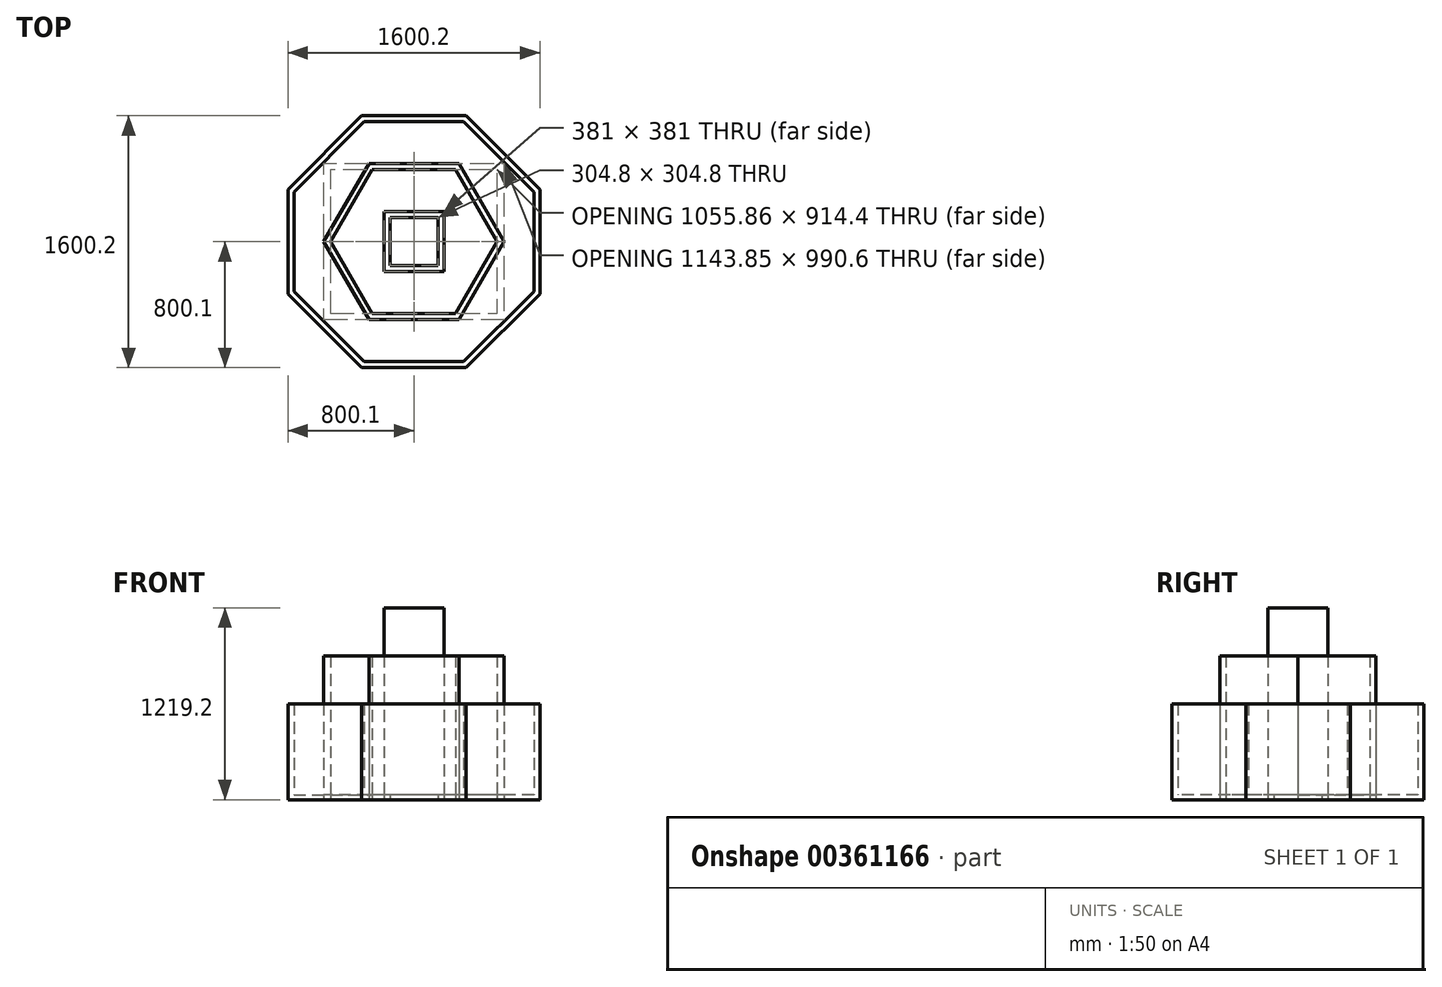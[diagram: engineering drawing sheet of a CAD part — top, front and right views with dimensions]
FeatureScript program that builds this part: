
annotation { "Feature Type Name" : "Feature", "Feature Type Description" : "" }
export const myFeature = defineFeature(function(context is Context, id is Id, definition is map)
    precondition{}
    {
        {
            var Q0;
            Q0=qCreatedBy(makeId("Top.planeOp"),FACE);
            var sketch = newSketch(context, id + "F0", { "sketchPlane" : qUnion([Q0])});
            skCircle(sketch, "E0.cCircle", {"center": v(0, 0) * mm, "radius": 762 * mm, "construction": true});
            skLineSegment(sketch, "E0.0", {"start": v(315.63, -762) * mm, "end": v(-315.63, -762) * mm});
            skLineSegment(sketch, "E0.1", {"start": v(-315.63, -762) * mm, "end": v(-762, -315.63) * mm});
            skLineSegment(sketch, "E0.2", {"start": v(-762, -315.63) * mm, "end": v(-762, 315.63) * mm});
            skLineSegment(sketch, "E0.3", {"start": v(-762, 315.63) * mm, "end": v(-315.63, 762) * mm});
            skLineSegment(sketch, "E0.4", {"start": v(-315.63, 762) * mm, "end": v(315.63, 762) * mm});
            skLineSegment(sketch, "E0.5", {"start": v(315.63, 762) * mm, "end": v(762, 315.63) * mm});
            skLineSegment(sketch, "E0.6", {"start": v(762, 315.63) * mm, "end": v(762, -315.63) * mm});
            skLineSegment(sketch, "E0.7", {"start": v(762, -315.63) * mm, "end": v(315.63, -762) * mm});
            skPoint(sketch, "E0.0.midPoint", {"position": v(0, -762) * mm});
            skCircle(sketch, "E1.cCircle", {"center": v(0, 0) * mm, "radius": 457.2 * mm, "construction": true});
            skLineSegment(sketch, "E1.0", {"start": v(263.96, -457.2) * mm, "end": v(-263.96, -457.2) * mm});
            skLineSegment(sketch, "E1.1", {"start": v(-263.96, -457.2) * mm, "end": v(-527.93, 0) * mm});
            skLineSegment(sketch, "E1.2", {"start": v(-527.93, 0) * mm, "end": v(-263.96, 457.2) * mm});
            skLineSegment(sketch, "E1.3", {"start": v(-263.96, 457.2) * mm, "end": v(263.96, 457.2) * mm});
            skLineSegment(sketch, "E1.4", {"start": v(263.96, 457.2) * mm, "end": v(527.93, 0) * mm});
            skLineSegment(sketch, "E1.5", {"start": v(527.93, 0) * mm, "end": v(263.96, -457.2) * mm});
            skPoint(sketch, "E1.0.midPoint", {"position": v(0, -457.2) * mm});
            skCircle(sketch, "E2.cCircle", {"center": v(0, 0) * mm, "radius": 152.4 * mm, "construction": true});
            skLineSegment(sketch, "E2.0", {"start": v(152.4, -152.4) * mm, "end": v(-152.4, -152.4) * mm});
            skLineSegment(sketch, "E2.1", {"start": v(-152.4, -152.4) * mm, "end": v(-152.4, 152.4) * mm});
            skLineSegment(sketch, "E2.2", {"start": v(-152.4, 152.4) * mm, "end": v(152.4, 152.4) * mm});
            skLineSegment(sketch, "E2.3", {"start": v(152.4, 152.4) * mm, "end": v(152.4, -152.4) * mm});
            skPoint(sketch, "E2.0.midPoint", {"position": v(0, -152.4) * mm});
            skPoint(sketch, "E3", {"position": v(0, 152.4) * mm});
            skPoint(sketch, "E4", {"position": v(0, 457.2) * mm});
            skPoint(sketch, "E5", {"position": v(0, 762) * mm});
            skCircle(sketch, "E6.cCircle", {"center": v(0, 0) * mm, "radius": 800.1 * mm, "construction": true});
            skLineSegment(sketch, "E6.0", {"start": v(331.41, -800.1) * mm, "end": v(-331.41, -800.1) * mm});
            skLineSegment(sketch, "E6.1", {"start": v(-331.41, -800.1) * mm, "end": v(-800.1, -331.41) * mm});
            skLineSegment(sketch, "E6.2", {"start": v(-800.1, -331.41) * mm, "end": v(-800.1, 331.41) * mm});
            skLineSegment(sketch, "E6.3", {"start": v(-800.1, 331.41) * mm, "end": v(-331.41, 800.1) * mm});
            skLineSegment(sketch, "E6.4", {"start": v(-331.41, 800.1) * mm, "end": v(331.41, 800.1) * mm});
            skLineSegment(sketch, "E6.5", {"start": v(331.41, 800.1) * mm, "end": v(800.1, 331.41) * mm});
            skLineSegment(sketch, "E6.6", {"start": v(800.1, 331.41) * mm, "end": v(800.1, -331.41) * mm});
            skLineSegment(sketch, "E6.7", {"start": v(800.1, -331.41) * mm, "end": v(331.41, -800.1) * mm});
            skPoint(sketch, "E6.0.midPoint", {"position": v(0, -800.1) * mm});
            skPoint(sketch, "E7", {"position": v(0, 800.1) * mm});
            skCircle(sketch, "E8.cCircle", {"center": v(0, 0) * mm, "radius": 495.3 * mm, "construction": true});
            skLineSegment(sketch, "E8.0", {"start": v(285.96, -495.3) * mm, "end": v(-285.96, -495.3) * mm});
            skLineSegment(sketch, "E8.1", {"start": v(-285.96, -495.3) * mm, "end": v(-571.92, 0) * mm});
            skLineSegment(sketch, "E8.2", {"start": v(-571.92, 0) * mm, "end": v(-285.96, 495.3) * mm});
            skLineSegment(sketch, "E8.3", {"start": v(-285.96, 495.3) * mm, "end": v(285.96, 495.3) * mm});
            skLineSegment(sketch, "E8.4", {"start": v(285.96, 495.3) * mm, "end": v(571.92, 0) * mm});
            skLineSegment(sketch, "E8.5", {"start": v(571.92, 0) * mm, "end": v(285.96, -495.3) * mm});
            skPoint(sketch, "E8.0.midPoint", {"position": v(0, -495.3) * mm});
            skPoint(sketch, "E9", {"position": v(0, 495.3) * mm});
            skCircle(sketch, "E10.cCircle", {"center": v(0, 0) * mm, "radius": 190.5 * mm, "construction": true});
            skLineSegment(sketch, "E10.0", {"start": v(190.5, -190.5) * mm, "end": v(-190.5, -190.5) * mm});
            skLineSegment(sketch, "E10.1", {"start": v(-190.5, -190.5) * mm, "end": v(-190.5, 190.5) * mm});
            skLineSegment(sketch, "E10.2", {"start": v(-190.5, 190.5) * mm, "end": v(190.5, 190.5) * mm});
            skLineSegment(sketch, "E10.3", {"start": v(190.5, 190.5) * mm, "end": v(190.5, -190.5) * mm});
            skPoint(sketch, "E10.0.midPoint", {"position": v(0, -190.5) * mm});
            skPoint(sketch, "E11", {"position": v(0, 190.5) * mm});
            skSolve(sketch);
        }
        {
            var Q0;
            Q0=makeQuery(id+"F0.imprint","IMPRINT",FACE,{"disambiguationData":[TD([[makeQuery(id+"F0.imprint","IMPRINT",EDGE,{"derivedFrom":sQuery(id+"F0.wireOp",EDGE,"E0.0")}),-1.0]])]});
            var Q1;
            Q1=makeQuery(id+"F0.imprint","IMPRINT",FACE,{"disambiguationData":[TD([[makeQuery(id+"F0.imprint","IMPRINT",EDGE,{"derivedFrom":sQuery(id+"F0.wireOp",EDGE,"E1.0")}),-1.0]])]});
            var Q2;
            Q2=makeQuery(id+"F0.imprint","IMPRINT",FACE,{"disambiguationData":[TD([[makeQuery(id+"F0.imprint","IMPRINT",EDGE,{"derivedFrom":sQuery(id+"F0.wireOp",EDGE,"E2.0")}),-1.0]])]});
            extrude(context, id + "F1", {"entities" : qUnion([Q0, Q1, Q2]), "depth" : 30.48 * mm});
        }
        {
            var Q0;
            Q0=makeQuery(id+"F0.imprint","IMPRINT",FACE,{"disambiguationData":[TD([[makeQuery(id+"F0.imprint","IMPRINT",EDGE,{"derivedFrom":sQuery(id+"F0.wireOp",EDGE,"E2.0")}),1.0]])]});
            extrude(context, id + "F2", {"entities" : qUnion([Q0]), "depth" : 1219.2 * mm});
        }
        {
            var Q0;
            Q0=makeQuery(id+"F0.imprint","IMPRINT",FACE,{"disambiguationData":[TD([[makeQuery(id+"F0.imprint","IMPRINT",EDGE,{"derivedFrom":sQuery(id+"F0.wireOp",EDGE,"E1.0")}),1.0]])]});
            extrude(context, id + "F3", {"entities" : qUnion([Q0]), "depth" : 914.4 * mm});
        }
        {
            var Q0;
            Q0=makeQuery(id+"F0.imprint","IMPRINT",FACE,{"disambiguationData":[TD([[makeQuery(id+"F0.imprint","IMPRINT",EDGE,{"derivedFrom":sQuery(id+"F0.wireOp",EDGE,"E0.0")}),1.0]])]});
            extrude(context, id + "F4", {"entities" : qUnion([Q0]), "operationType" : NewBodyOperationType.ADD, "depth" : 609.6 * mm});
        }
    });
